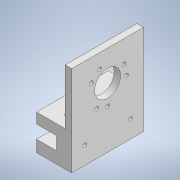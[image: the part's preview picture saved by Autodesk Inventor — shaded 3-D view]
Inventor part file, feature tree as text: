
AUTODESK INVENTOR PART (.ipt)
format: ipt  version: 2022 (Build 260153000, 153)  size: 179,712 bytes
history: native  units: in
note: dims shown in document units (in); Inventor stores cm internally (conversion verified against a paired STEP export)
features: extrude x8, sketch x8, reference x7, other x3
ambient origin geometry x8: Origin, YZ Plane, XZ Plane, XY Plane, X Axis, Y Axis, Z Axis, Center Point
bodies: Solid1 (feature_tree)
feature tree (26):
  extrude  "Extrusion1"  Depth=0.1181in
  extrude  "Extrusion2"  Depth=0.1181in
  extrude  "Extrusion3"  Depth=0.3937in
  extrude  "Extrusion4"  Depth=0.315in TaperAngle=0.0deg
  extrude  "Extrusion5"  Depth=1.6654in TaperAngle=0.0deg
  extrude  "Extrusion6"  Depth=0.748in
  extrude  "Extrusion7"  Depth=1.6654in TaperAngle=0.0deg
  extrude  "Extrusion8"  Depth=1.6654in TaperAngle=0.0deg
  sketch  "Sketch1"  dims[d1=0.1181in d2=0.1181in]
  reference  "Reference1"
  sketch  "Sketch2"  dims[d3=0.1181in d4=0.1181in]
  sketch  "Sketch3"  dims[d5=2.1654in d6=0.0in d7=0.3937in]
  sketch  "Sketch4"  dims[d8=0.315in d9=0.6029in d10=0.0in]
  sketch  "Sketch5"  dims[d11=0.1969in d12=1.6654in d13=0.0in]
  sketch  "Sketch6"  dims[d14=1.4173in d15=0.748in]
  reference  "Reference2"
  reference  "Reference3"
  reference  "Reference4"
  reference  "Reference5"
  reference  "Reference6"
  reference  "Reference7"
  sketch  "Sketch7"  dims[d16=0.2362in d17=1.6654in d18=0.0in]
  sketch  "Sketch8"  dims[d19=0.7874in d20=1.6654in d21=0.0in d22=1.6654in d23=0.0in d24=0.1181in d25=0.1181in d26=0.3937in d27=0.3937in d28=0.3937in d29=0.0in d30=0.1181in d31=0.1181in d32=0.3937in d33=0.3937in d34=0.0in d35=0.0in]
  parser-record x1  (decoder bookkeeping rows leaked as tree rows — omitted from the tree; the rows remain in map.json)
  other  "model.iam"
  other  "arm:1"
note: 1 file-system path scrubbed to <path> (originals preserved in map.json)
